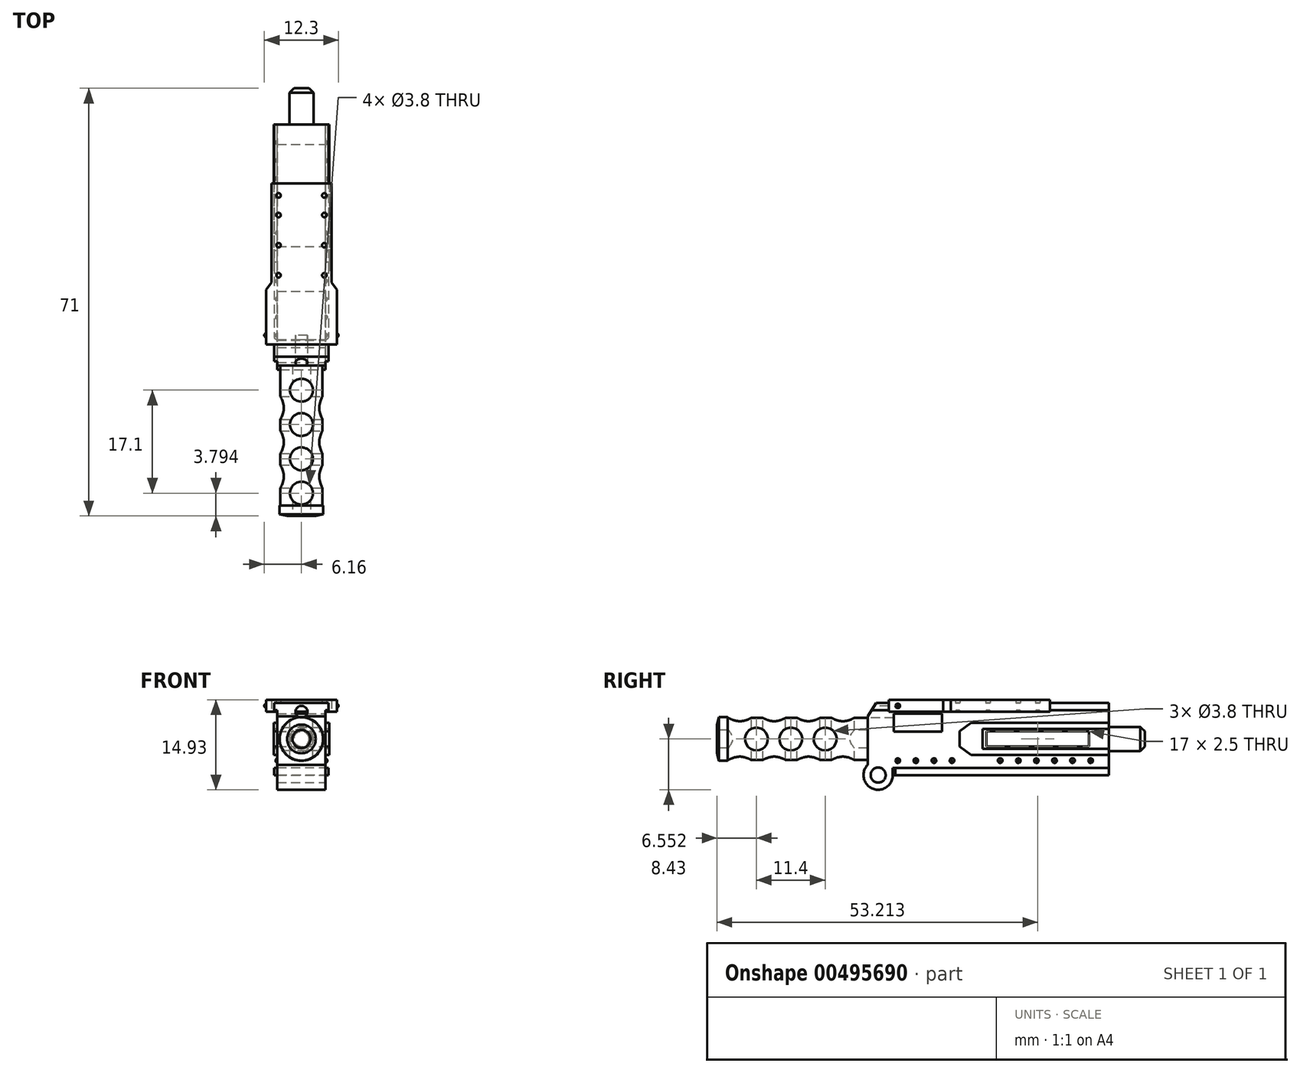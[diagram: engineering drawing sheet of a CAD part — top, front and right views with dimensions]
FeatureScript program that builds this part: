
annotation { "Feature Type Name" : "Feature", "Feature Type Description" : "" }
export const myFeature = defineFeature(function(context is Context, id is Id, definition is map)
    precondition{}
    {
        {
            var Q0;
            Q0=qCreatedBy(makeId("Front.planeOp"),FACE);
            var sketch = newSketch(context, id + "F0", { "sketchPlane" : qUnion([Q0])});
            skLineSegment(sketch, "E0.bottom", {"start": v(4, 6) * mm, "end": v(-4, 6) * mm});
            skLineSegment(sketch, "E0.top", {"start": v(4, -6) * mm, "end": v(-4, -6) * mm});
            skLineSegment(sketch, "E0.left", {"start": v(4, 6) * mm, "end": v(4, -6) * mm});
            skLineSegment(sketch, "E0.right", {"start": v(-4, 6) * mm, "end": v(-4, -6) * mm});
            skPoint(sketch, "E0.middle", {"position": v(0, 0) * mm});
            skSolve(sketch);
        }
        {
            var Q0;
            Q0=makeQuery(id+"F0.imprint","IMPRINT",FACE,{"disambiguationData":[TD([[makeQuery(id+"F0.imprint","IMPRINT",EDGE,{"derivedFrom":sQuery(id+"F0.wireOp",EDGE,"E0.bottom")}),1.0]])]});
            extrude(context, id + "F1", {"entities" : qUnion([Q0]), "depth" : 40 * mm});
        }
        {
            var Q0;
            Q0=makeQuery(id+"F1.opExtrude","CAP_FACE",FACE,{"disambiguationData":[OSD([sQuery(id+"F0.wireOp",EDGE,"E0.bottom"),sQuery(id+"F0.wireOp",EDGE,"E0.top"),sQuery(id+"F0.wireOp",EDGE,"E0.left"),sQuery(id+"F0.wireOp",EDGE,"E0.right")])],"isStart":false});
            var sketch = newSketch(context, id + "F2", { "sketchPlane" : qUnion([Q0])});
            skCircle(sketch, "E1", {"center": v(0, 0) * mm, "radius": 3.5 * mm});
            skSolve(sketch);
        }
        {
            var Q0;
            Q0=qSketchRegion(id+"F2",true);
            extrude(context, id + "F3", {"entities" : qUnion([Q0]), "operationType" : NewBodyOperationType.ADD, "depth" : 25 * mm});
        }
        {
            var Q0;
            Q0=makeQuery(id+"F3.opExtrude","CAP_FACE",FACE,{"disambiguationData":[OSD([sQuery(id+"F2.wireOp",EDGE,"E1")])],"isStart":false});
            var sketch = newSketch(context, id + "F4", { "sketchPlane" : qUnion([Q0])});
            skCircle(sketch, "E2", {"center": v(0, 0) * mm, "radius": 1.5 * mm});
            skSolve(sketch);
        }
        {
            var Q0;
            Q0=makeQuery(id+"F4.imprint","IMPRINT",FACE,{"disambiguationData":[TD([[makeQuery(id+"F4.imprint","IMPRINT",EDGE,{"derivedFrom":sQuery(id+"F4.wireOp",EDGE,"E2")}),-1.0]])]});
            var sketch = newSketch(context, id + "F5", { "sketchPlane" : qUnion([Q0])});
            skCircle(sketch, "E3", {"center": v(0, 0) * mm, "radius": 3.62 * mm});
            skSolve(sketch);
        }
        {
            var Q0;
            Q0=qSketchRegion(id+"F5",true);
            extrude(context, id + "F6", {"entities" : qUnion([Q0]), "operationType" : NewBodyOperationType.ADD, "oppositeDirection" : true, "depth" : 1.75 * mm, "offsetDistance" : 25 * mm});
        }
        {
            var Q0;
            Q0=qSketchRegion(id+"F4",true);
            var Q1;
            Q1=makeQuery(id+"F1.opExtrude","CAP_FACE",FACE,{"disambiguationData":[OSD([sQuery(id+"F0.wireOp",EDGE,"E0.bottom"),sQuery(id+"F0.wireOp",EDGE,"E0.top"),sQuery(id+"F0.wireOp",EDGE,"E0.left"),sQuery(id+"F0.wireOp",EDGE,"E0.right")])],"isStart":false});
            extrude(context, id + "F7", {"entities" : qUnion([Q0]), "operationType" : NewBodyOperationType.REMOVE, "endBound" : BoundingType.UP_TO_SURFACE, "oppositeDirection" : true, "endBoundEntityFace" : qUnion([Q1]), "offsetDistance" : 25 * mm, "depth" : 35 * mm, "hasSecondDirection" : true, "secondDirectionOppositeDirection" : false, "secondDirectionDepth" : .5 * mm});
        }
        {
            var Q0;
            Q0=makeQuery(id+"F1.opExtrude","SWEPT_FACE",FACE,{"disambiguationData":[OSD([sQuery(id+"F0.wireOp",EDGE,"E0.left")])]});
            var sketch = newSketch(context, id + "F8", { "sketchPlane" : qUnion([Q0])});
            skCircle(sketch, "E4", {"center": v(-38.25, -6) * mm, "radius": 2.43 * mm});
            skSolve(sketch);
        }
        {
            var Q0;
            {var subQ0=sQuery(id+"F0.wireOp",EDGE,"E0.left");var subQ1=makeQuery(id+"F1.opExtrude","CAP_EDGE",EDGE,{"disambiguationData":[OSD([subQ0])],"isStart":false});var subQ4=sQuery(id+"F8.wireOp",EDGE,"E4");var subQ5=makeQuery(id+"F8.imprint","INTERSECT",VERTEX,{"derivedFrom":[subQ1,subQ4]});Q0=makeQuery(id+"F8.imprint","IMPRINT",FACE,{"disambiguationData":[TD([[makeQuery(id+"F8.imprint","IMPRINT",EDGE,{"disambiguationData":[TD([[subQ5,-1.0]])],"derivedFrom":subQ4}),1.0]])]});}
            extrude(context, id + "F9", {"entities" : qUnion([Q0]), "operationType" : NewBodyOperationType.ADD, "oppositeDirection" : true, "depth" : 8 * mm});
        }
        {
            var Q0;
            {var subQ0=sQuery(id+"F0.wireOp",EDGE,"E0.left");Q0=makeQuery(id+"F9.boolean.opBoolean","MERGE",FACE,{"derivedFrom":[makeQuery(id+"F1.opExtrude","SWEPT_FACE",FACE,{"disambiguationData":[OSD([subQ0])]}),makeQuery(id+"F9.opExtrude","CAP_FACE",FACE,{"disambiguationData":[OSD([sQuery(id+"F0.wireOp",EDGE,"E0.top"),subQ0,sQuery(id+"F8.wireOp",EDGE,"E4")])],"isStart":true})]});}
            var sketch = newSketch(context, id + "F10", { "sketchPlane" : qUnion([Q0])});
            skCircle(sketch, "E5", {"center": v(-38.25, -6) * mm, "radius": 1.25 * mm});
            skSolve(sketch);
        }
        {
            var Q0;
            Q0=qSketchRegion(id+"F10",true);
            extrude(context, id + "F11", {"entities" : qUnion([Q0]), "operationType" : NewBodyOperationType.REMOVE, "endBound" : BoundingType.THROUGH_ALL, "oppositeDirection" : true, "depth" : 25 * mm});
        }
        {
            var Q0;
            {var subQ0=sQuery(id+"F0.wireOp",EDGE,"E0.left");Q0=makeQuery(id+"F9.boolean.opBoolean","MERGE",FACE,{"derivedFrom":[makeQuery(id+"F1.opExtrude","SWEPT_FACE",FACE,{"disambiguationData":[OSD([subQ0])]}),makeQuery(id+"F9.opExtrude","CAP_FACE",FACE,{"disambiguationData":[OSD([sQuery(id+"F0.wireOp",EDGE,"E0.top"),subQ0,sQuery(id+"F8.wireOp",EDGE,"E4")])],"isStart":true})]});}
            var sketch = newSketch(context, id + "F12", { "sketchPlane" : qUnion([Q0])});
            skLineSegment(sketch, "E6", {"start": v(-40, 6) * mm, "end": v(-35.67, 6) * mm});
            skLineSegment(sketch, "E7", {"start": v(-35.67, 6) * mm, "end": v(-35.67, 4.2) * mm});
            skLineSegment(sketch, "E8.bottom", {"start": v(-35.67, 4.2) * mm, "end": v(-27.67, 4.2) * mm});
            skLineSegment(sketch, "E8.top", {"start": v(-35.67, 1.2) * mm, "end": v(-27.67, 1.2) * mm});
            skLineSegment(sketch, "E8.left", {"start": v(-35.67, 4.2) * mm, "end": v(-35.67, 1.2) * mm});
            skLineSegment(sketch, "E8.right", {"start": v(-27.67, 4.2) * mm, "end": v(-27.67, 1.2) * mm});
            skLineSegment(sketch, "E9.bottom", {"start": v(-20.29, -1.25) * mm, "end": v(-3.29, -1.25) * mm});
            skLineSegment(sketch, "E9.top", {"start": v(-20.29, 1.25) * mm, "end": v(-3.29, 1.25) * mm});
            skLineSegment(sketch, "E9.left", {"start": v(-20.29, -1.25) * mm, "end": v(-20.29, 1.25) * mm});
            skLineSegment(sketch, "E9.right", {"start": v(-3.29, -1.25) * mm, "end": v(-3.29, 1.25) * mm});
            skPoint(sketch, "E9.middle", {"position": v(-11.79, 0) * mm});
            skSolve(sketch);
        }
        {
            var Q0;
            Q0=makeQuery(id+"F12.imprint","IMPRINT",FACE,{"disambiguationData":[TD([[makeQuery(id+"F12.imprint","IMPRINT",EDGE,{"derivedFrom":sQuery(id+"F12.wireOp",EDGE,"E9.bottom")}),1.0]])]});
            var Q1;
            Q1=makeQuery(id+"F12.imprint","IMPRINT",FACE,{"disambiguationData":[TD([[makeQuery(id+"F12.imprint","IMPRINT",EDGE,{"derivedFrom":sQuery(id+"F12.wireOp",EDGE,"E8.bottom")}),-1.0]])]});
            extrude(context, id + "F13", {"entities" : qUnion([Q0, Q1]), "operationType" : NewBodyOperationType.REMOVE, "endBound" : BoundingType.THROUGH_ALL, "oppositeDirection" : true, "depth" : 25 * mm});
        }
        {
            var Q0;
            Q0=makeQuery(id+"F1.opExtrude","SWEPT_FACE",FACE,{"disambiguationData":[OSD([sQuery(id+"F0.wireOp",EDGE,"E0.bottom")])]});
            var sketch = newSketch(context, id + "F14", { "sketchPlane" : qUnion([Q0])});
            skLineSegment(sketch, "E10", {"start": v(4, -29.35) * mm, "end": v(-4, -29.35) * mm, "construction": true});
            skLineSegment(sketch, "E11", {"start": v(4, -29.35) * mm, "end": v(4.5, -29.35) * mm});
            skLineSegment(sketch, "E12", {"start": v(-4, -29.35) * mm, "end": v(-4.5, -29.35) * mm});
            skLineSegment(sketch, "E13.bottom", {"start": v(4.5, -40) * mm, "end": v(-4.5, -40) * mm});
            skLineSegment(sketch, "E13.top", {"start": v(4.5, 0) * mm, "end": v(-4.5, 0) * mm});
            skLineSegment(sketch, "E13.left", {"start": v(4.5, -40) * mm, "end": v(4.5, 0) * mm});
            skLineSegment(sketch, "E13.right", {"start": v(-4.5, -40) * mm, "end": v(-4.5, 0) * mm});
            skSolve(sketch);
        }
        {
            var Q0;
            Q0=qSketchRegion(id+"F14",true);
            extrude(context, id + "F15", {"entities" : qUnion([Q0]), "operationType" : NewBodyOperationType.ADD, "oppositeDirection" : true, "depth" : 1.2 * mm});
        }
        {
            var Q0;
            Q0=makeQuery(id+"F1.opExtrude","SWEPT_FACE",FACE,{"disambiguationData":[OSD([sQuery(id+"F0.wireOp",EDGE,"E0.top")])]});
            var sketch = newSketch(context, id + "F16", { "sketchPlane" : qUnion([Q0])});
            skLineSegment(sketch, "E14", {"start": v(4, 0) * mm, "end": v(4.5, 0) * mm});
            skLineSegment(sketch, "E15", {"start": v(-4, 35.82) * mm, "end": v(-4.5, 35.82) * mm});
            skLineSegment(sketch, "E16.bottom", {"start": v(4.5, 0) * mm, "end": v(-4.5, 0) * mm});
            skLineSegment(sketch, "E16.top", {"start": v(4.5, 35.82) * mm, "end": v(-4.5, 35.82) * mm});
            skLineSegment(sketch, "E16.left", {"start": v(4.5, 0) * mm, "end": v(4.5, 35.82) * mm});
            skLineSegment(sketch, "E16.right", {"start": v(-4.5, 0) * mm, "end": v(-4.5, 35.82) * mm});
            skLineSegment(sketch, "E17", {"start": v(4, 35.82) * mm, "end": v(4.5, 35.38) * mm});
            skLineSegment(sketch, "E18", {"start": v(-4.5, 35.38) * mm, "end": v(-4, 35.82) * mm});
            skSolve(sketch);
        }
        {
            var Q0;
            {var subQ4=sQuery(id+"F16.wireOp",EDGE,"E17");Q0=makeQuery(id+"F16.imprint","IMPRINT",FACE,{"disambiguationData":[TD([[makeQuery(id+"F16.imprint","IMPRINT",EDGE,{"derivedFrom":subQ4}),-1.0]])]});}
            var Q1;
            {var subQ1=sQuery(id+"F0.wireOp",EDGE,"E0.top");var subQ2=makeQuery(id+"F1.opExtrude","SWEPT_EDGE",EDGE,{"disambiguationData":[OSD([subQ1,sQuery(id+"F0.wireOp",EDGE,"E0.left")])]});Q1=makeQuery(id+"F16.imprint","IMPRINT",FACE,{"disambiguationData":[TD([[makeQuery(id+"F16.imprint","IMPRINT",EDGE,{"derivedFrom":subQ2}),-1.0]])]});}
            var Q2;
            {var subQ4=sQuery(id+"F16.wireOp",EDGE,"E18");Q2=makeQuery(id+"F16.imprint","IMPRINT",FACE,{"disambiguationData":[TD([[makeQuery(id+"F16.imprint","IMPRINT",EDGE,{"derivedFrom":subQ4}),-1.0]])]});}
            extrude(context, id + "F17", {"entities" : qUnion([Q0, Q1, Q2]), "operationType" : NewBodyOperationType.ADD, "oppositeDirection" : true, "depth" : 1.2 * mm});
        }
        {
            var Q0;
            Q0=makeQuery(id+"F15.boolean.opBoolean","MERGE",FACE,{"derivedFrom":[makeQuery(id+"F1.opExtrude","CAP_FACE",FACE,{"disambiguationData":[OSD([sQuery(id+"F0.wireOp",EDGE,"E0.bottom"),sQuery(id+"F0.wireOp",EDGE,"E0.top"),sQuery(id+"F0.wireOp",EDGE,"E0.left"),sQuery(id+"F0.wireOp",EDGE,"E0.right")])],"isStart":false}),makeQuery(id+"F15.opExtrude","SWEPT_FACE",FACE,{"disambiguationData":[OSD([sQuery(id+"F14.wireOp",EDGE,"E13.bottom")])]})]});
            var sketch = newSketch(context, id + "F18", { "sketchPlane" : qUnion([Q0])});
            skPoint(sketch, "E19.endSnap0", {"position": v(0, 6) * mm});
            skCircle(sketch, "E20", {"center": v(0, 4.5) * mm, "radius": 1 * mm});
            skSolve(sketch);
        }
        {
            var Q0;
            Q0=makeQuery(id+"F18.imprint","IMPRINT",FACE,{"disambiguationData":[TD([[makeQuery(id+"F18.imprint","IMPRINT",EDGE,{"derivedFrom":sQuery(id+"F18.wireOp",EDGE,"E20")}),1.0]])]});
            var Q1;
            Q1=sQuery(id+"F18.wireOp",EDGE,"E20");
            extrude(context, id + "F19", {"entities" : qUnion([Q0]), "operationType" : NewBodyOperationType.REMOVE, "surfaceEntities" : qUnion([Q1]), "oppositeDirection" : true, "offsetDistance" : 25 * mm, "depth" : 5 * mm});
        }
        {
            var Q0;
            Q0=makeQuery(id+"F10.imprint","IMPRINT",FACE,{"disambiguationData":[TD([[makeQuery(id+"F10.imprint","IMPRINT",EDGE,{"derivedFrom":sQuery(id+"F10.wireOp",EDGE,"E5")}),-1.0]])]});
            var sketch = newSketch(context, id + "F20", { "sketchPlane" : qUnion([Q0])});
            skLineSegment(sketch, "E21", {"start": v(0, 1.65) * mm, "end": v(-20.95, 1.65) * mm});
            skLineSegment(sketch, "E22", {"start": v(-20.95, 1.65) * mm, "end": v(-20.95, 0) * mm});
            skLineSegment(sketch, "E23.MirrorCS", {"start": v(0, -1.65) * mm, "end": v(-20.95, -1.65) * mm});
            skLineSegment(sketch, "E24.MirrorCS", {"start": v(-20.95, -1.65) * mm, "end": v(-20.95, 0) * mm});
            skLineSegment(sketch, "E25", {"start": v(0, 1.65) * mm, "end": v(0, 2.68) * mm});
            skLineSegment(sketch, "E26", {"start": v(0, 2.68) * mm, "end": v(-22.85, 2.68) * mm});
            skLineSegment(sketch, "E27", {"start": v(-22.85, 2.68) * mm, "end": v(-24.71, 1.26) * mm});
            skLineSegment(sketch, "E28", {"start": v(-24.71, 1.26) * mm, "end": v(-24.71, 0) * mm});
            skLineSegment(sketch, "E29.MirrorCS", {"start": v(0, -2.68) * mm, "end": v(-22.85, -2.68) * mm});
            skLineSegment(sketch, "E30.MirrorCS", {"start": v(-22.85, -2.68) * mm, "end": v(-24.71, -1.26) * mm});
            skLineSegment(sketch, "E31.MirrorCS", {"start": v(-24.71, -1.26) * mm, "end": v(-24.71, 0) * mm});
            skLineSegment(sketch, "E32", {"start": v(0, -2.68) * mm, "end": v(0, -1.65) * mm});
            skSolve(sketch);
        }
        {
            var Q0;
            Q0=qSketchRegion(id+"F20",true);
            extrude(context, id + "F21", {"entities" : qUnion([Q0]), "operationType" : NewBodyOperationType.ADD, "depth" : .6 * mm, "hasSecondDirection" : true, "secondDirectionOppositeDirection" : true, "secondDirectionDepth" : 8.6 * mm});
        }
        {
            var Q0;
            Q0=makeQuery(id+"F21.boolean.opBoolean","MERGE",FACE,{"derivedFrom":[makeQuery(id+"F17.boolean.opBoolean","MERGE",FACE,{"derivedFrom":[makeQuery(id+"F15.boolean.opBoolean","MERGE",FACE,{"derivedFrom":[makeQuery(id+"F1.opExtrude","CAP_FACE",FACE,{"disambiguationData":[OSD([sQuery(id+"F0.wireOp",EDGE,"E0.bottom"),sQuery(id+"F0.wireOp",EDGE,"E0.top"),sQuery(id+"F0.wireOp",EDGE,"E0.left"),sQuery(id+"F0.wireOp",EDGE,"E0.right")])],"isStart":true}),makeQuery(id+"F15.opExtrude","SWEPT_FACE",FACE,{"disambiguationData":[OSD([sQuery(id+"F14.wireOp",EDGE,"E13.top")])]})]}),makeQuery(id+"F17.opExtrude","SWEPT_FACE",FACE,{"disambiguationData":[OSD([sQuery(id+"F16.wireOp",EDGE,"E16.bottom")])]})]}),makeQuery(id+"F21.opExtrude","SWEPT_FACE",FACE,{"disambiguationData":[OSD([sQuery(id+"F20.wireOp",EDGE,"E25")])]}),makeQuery(id+"F21.opExtrude","SWEPT_FACE",FACE,{"disambiguationData":[OSD([sQuery(id+"F20.wireOp",EDGE,"E32")])]})]});
            var sketch = newSketch(context, id + "F22", { "sketchPlane" : qUnion([Q0])});
            skCircle(sketch, "E33", {"center": v(0, 0) * mm, "radius": 2 * mm});
            skSolve(sketch);
        }
        {
            var Q0;
            Q0=qCreatedBy(makeId("Top.planeOp"),FACE);
            var sketch = newSketch(context, id + "F23", { "sketchPlane" : qUnion([Q0])});
            skLineSegment(sketch, "E34", {"start": v(0, -65) * mm, "end": v(0, -63.1) * mm});
            skLineSegment(sketch, "E35", {"start": v(0, -63.1) * mm, "end": v(0, -61.2) * mm});
            skLineSegment(sketch, "E36", {"start": v(0, -61.2) * mm, "end": v(0, -59.3) * mm});
            skLineSegment(sketch, "E37", {"start": v(0, -59.3) * mm, "end": v(0, -57.4) * mm});
            skLineSegment(sketch, "E38", {"start": v(0, -57.4) * mm, "end": v(0, -55.5) * mm});
            skLineSegment(sketch, "E39", {"start": v(0, -55.5) * mm, "end": v(0, -53.6) * mm});
            skLineSegment(sketch, "E40", {"start": v(0, -53.6) * mm, "end": v(0, -51.7) * mm});
            skLineSegment(sketch, "E41", {"start": v(0, -51.7) * mm, "end": v(0, -49.8) * mm});
            skLineSegment(sketch, "E42", {"start": v(0, -49.8) * mm, "end": v(0, -47.9) * mm});
            skLineSegment(sketch, "E43", {"start": v(0, -47.9) * mm, "end": v(0, -46) * mm});
            skLineSegment(sketch, "E44", {"start": v(0, -46) * mm, "end": v(0, -44.1) * mm});
            skLineSegment(sketch, "E45", {"start": v(0, -44.1) * mm, "end": v(0, -42.2) * mm});
            skCircle(sketch, "E46", {"center": v(0, -61.2) * mm, "radius": 1.9 * mm});
            skCircle(sketch, "E47", {"center": v(0, -55.5) * mm, "radius": 1.9 * mm});
            skCircle(sketch, "E48", {"center": v(0, -49.8) * mm, "radius": 1.9 * mm});
            skCircle(sketch, "E49", {"center": v(0, -44.1) * mm, "radius": 1.9 * mm});
            skSolve(sketch);
        }
        {
            var Q0;
            Q0=qSketchRegion(id+"F23",true);
            extrude(context, id + "F24", {"entities" : qUnion([Q0]), "operationType" : NewBodyOperationType.REMOVE, "oppositeDirection" : true, "depth" : 6 * mm, "hasSecondDirection" : true, "secondDirectionOppositeDirection" : false, "secondDirectionDepth" : 6 * mm});
        }
        {
            var Q0;
            Q0=qCreatedBy(makeId("Right.planeOp"),FACE);
            var sketch = newSketch(context, id + "F25", { "sketchPlane" : qUnion([Q0])});
            skLineSegment(sketch, "E50", {"start": v(-81.72, 0) * mm, "end": v(-78.97, 0) * mm});
            skLineSegment(sketch, "E51", {"start": v(-65, 0) * mm, "end": v(-62.25, 0) * mm});
            skLineSegment(sketch, "E52", {"start": v(-62.25, 0) * mm, "end": v(-60.35, 0) * mm});
            skLineSegment(sketch, "E53", {"start": v(-60.35, 0) * mm, "end": v(-58.45, 0) * mm});
            skLineSegment(sketch, "E54", {"start": v(-58.45, 0) * mm, "end": v(-56.55, 0) * mm});
            skLineSegment(sketch, "E55", {"start": v(-56.55, 0) * mm, "end": v(-54.65, 0) * mm});
            skLineSegment(sketch, "E56", {"start": v(-54.65, 0) * mm, "end": v(-52.75, 0) * mm});
            skLineSegment(sketch, "E57", {"start": v(-52.75, 0) * mm, "end": v(-50.85, 0) * mm});
            skLineSegment(sketch, "E58", {"start": v(-50.85, 0) * mm, "end": v(-48.95, 0) * mm});
            skLineSegment(sketch, "E59", {"start": v(-48.95, 0) * mm, "end": v(-47.05, 0) * mm});
            skLineSegment(sketch, "E60", {"start": v(-47.05, 0) * mm, "end": v(-45.15, 0) * mm});
            skCircle(sketch, "E61", {"center": v(-58.45, 0) * mm, "radius": 1.9 * mm});
            skCircle(sketch, "E62", {"center": v(-52.75, 0) * mm, "radius": 1.9 * mm});
            skCircle(sketch, "E63", {"center": v(-47.05, 0) * mm, "radius": 1.9 * mm});
            skLineSegment(sketch, "E64", {"start": v(-47.05, 0) * mm, "end": v(-47.05, 4.24) * mm});
            skSolve(sketch);
        }
        {
            var Q0;
            Q0=qSketchRegion(id+"F25",true);
            extrude(context, id + "F26", {"entities" : qUnion([Q0]), "operationType" : NewBodyOperationType.REMOVE, "endBound" : BoundingType.THROUGH_ALL, "oppositeDirection" : true, "depth" : 25 * mm, "hasSecondDirection" : true, "secondDirectionOppositeDirection" : false, "secondDirectionDepth" : 25 * mm});
        }
        {
            var Q0;
            Q0=qSketchRegion(id+"F22",true);
            extrude(context, id + "F27", {"entities" : qUnion([Q0]), "operationType" : NewBodyOperationType.ADD, "offsetDistance" : 25 * mm, "depth" : 6 * mm});
        }
        {
            var Q0;
            Q0=makeQuery(id+"F10.imprint","IMPRINT",FACE,{"disambiguationData":[TD([[makeQuery(id+"F10.imprint","IMPRINT",EDGE,{"derivedFrom":sQuery(id+"F10.wireOp",EDGE,"E5")}),-1.0]])]});
            var sketch = newSketch(context, id + "F28", { "sketchPlane" : qUnion([Q0])});
            skLineSegment(sketch, "E65", {"start": v(-40.01, 3.72) * mm, "end": v(-38.55, 6.02) * mm});
            skLineSegment(sketch, "E66", {"start": v(-38.55, 6.02) * mm, "end": v(-40.05, 6.02) * mm});
            skLineSegment(sketch, "E67", {"start": v(-40.05, 6.02) * mm, "end": v(-40.01, 3.72) * mm});
            skSolve(sketch);
        }
        {
            var Q0;
            Q0=qSketchRegion(id+"F28",true);
            extrude(context, id + "F29", {"entities" : qUnion([Q0]), "operationType" : NewBodyOperationType.REMOVE, "endBound" : BoundingType.THROUGH_ALL, "oppositeDirection" : true, "depth" : 25 * mm, "hasSecondDirection" : true, "secondDirectionBound" : SecondDirectionBoundingType.THROUGH_ALL, "secondDirectionOppositeDirection" : false, "secondDirectionDepth" : 25 * mm});
        }
        {
            var Q0;
            {var subQ1=sQuery(id+"F0.wireOp",EDGE,"E0.bottom");var subQ2=makeQuery(id+"F1.opExtrude","SWEPT_EDGE",EDGE,{"disambiguationData":[OSD([subQ1,sQuery(id+"F0.wireOp",EDGE,"E0.left")])]});var subQ7=sQuery(id+"F14.wireOp",EDGE,"E13.bottom");var subQ8=makeQuery(id+"F14.imprint","INTERSECT",VERTEX,{"derivedFrom":[subQ2,subQ7]});Q0=makeQuery(id+"F14.imprint","IMPRINT",FACE,{"disambiguationData":[TD([[makeQuery(id+"F14.imprint","IMPRINT",EDGE,{"disambiguationData":[TD([[subQ8,-1.0]])],"derivedFrom":subQ7}),-1.0]])]});}
            var sketch = newSketch(context, id + "F30", { "sketchPlane" : qUnion([Q0])});
            skLineSegment(sketch, "E68", {"start": v(0, -9.78) * mm, "end": v(-5, -9.78) * mm});
            skLineSegment(sketch, "E69", {"start": v(-5, -9.78) * mm, "end": v(-5, -26.2) * mm});
            skLineSegment(sketch, "E70", {"start": v(-5, -26.2) * mm, "end": v(-5.86, -27.45) * mm});
            skLineSegment(sketch, "E71", {"start": v(-5.86, -27.45) * mm, "end": v(-5.86, -36.5) * mm});
            skLineSegment(sketch, "E72", {"start": v(-5.86, -36.5) * mm, "end": v(0, -36.5) * mm});
            skLineSegment(sketch, "E73", {"start": v(0, 0) * mm, "end": v(0, -16.84) * mm, "construction": true});
            skLineSegment(sketch, "E74.MirrorCS", {"start": v(0, -9.78) * mm, "end": v(5, -9.78) * mm});
            skLineSegment(sketch, "E75.MirrorCS", {"start": v(5, -9.78) * mm, "end": v(5, -26.2) * mm});
            skLineSegment(sketch, "E76.MirrorCS", {"start": v(5.86, -36.5) * mm, "end": v(0, -36.5) * mm});
            skLineSegment(sketch, "E77.MirrorCS", {"start": v(5.86, -27.45) * mm, "end": v(5.86, -36.5) * mm});
            skLineSegment(sketch, "E78.MirrorCS", {"start": v(5, -26.2) * mm, "end": v(5.86, -27.45) * mm});
            skLineSegment(sketch, "E79", {"start": v(0, -9.78) * mm, "end": v(5, -9.78) * mm, "construction": true});
            skLineSegment(sketch, "E80", {"start": v(0, -9.78) * mm, "end": v(0, -11.78) * mm, "construction": true});
            skLineSegment(sketch, "E81", {"start": v(0, -11.78) * mm, "end": v(3.8, -11.78) * mm, "construction": true});
            skLineSegment(sketch, "E82", {"start": v(3.8, -11.78) * mm, "end": v(3.8, -15.04) * mm, "construction": true});
            skLineSegment(sketch, "E83", {"start": v(3.8, -15.04) * mm, "end": v(3.8, -17.54) * mm, "construction": true});
            skLineSegment(sketch, "E84", {"start": v(3.8, -17.54) * mm, "end": v(3.8, -20.04) * mm, "construction": true});
            skLineSegment(sketch, "E85", {"start": v(3.8, -20.04) * mm, "end": v(3.8, -22.54) * mm, "construction": true});
            skLineSegment(sketch, "E86", {"start": v(3.8, -22.54) * mm, "end": v(3.8, -25.04) * mm, "construction": true});
            skCircle(sketch, "E87", {"center": v(3.8, -11.78) * mm, "radius": 0.38 * mm});
            skCircle(sketch, "E88", {"center": v(3.8, -15.04) * mm, "radius": 0.38 * mm});
            skCircle(sketch, "E89", {"center": v(3.8, -20.04) * mm, "radius": 0.38 * mm});
            skCircle(sketch, "E90", {"center": v(3.8, -25.04) * mm, "radius": 0.38 * mm});
            skCircle(sketch, "E91.MirrorC", {"center": v(-3.8, -11.78) * mm, "radius": 0.38 * mm});
            skCircle(sketch, "E92.MirrorC", {"center": v(-3.8, -15.04) * mm, "radius": 0.38 * mm});
            skCircle(sketch, "E93.MirrorC", {"center": v(-3.8, -20.04) * mm, "radius": 0.38 * mm});
            skCircle(sketch, "E94.MirrorC", {"center": v(-3.8, -25.04) * mm, "radius": 0.38 * mm});
            skSolve(sketch);
        }
        {
            var Q0;
            Q0=qSketchRegion(id+"F30",true);
            extrude(context, id + "F31", {"entities" : qUnion([Q0]), "operationType" : NewBodyOperationType.ADD, "depth" : 0.5 * mm, "offsetDistance" : 25 * mm, "hasSecondDirection" : true, "secondDirectionOppositeDirection" : true, "secondDirectionDepth" : 1.5 * mm});
        }
        {
            var Q0;
            Q0=makeQuery(id+"F31.opExtrude","SWEPT_FACE",FACE,{"disambiguationData":[OSD([sQuery(id+"F30.wireOp",EDGE,"E71")])]});
            var sketch = newSketch(context, id + "F32", { "sketchPlane" : qUnion([Q0])});
            skLineSegment(sketch, "E95", {"start": v(36.5, 4.5) * mm, "end": v(36.5, 5.5) * mm, "construction": true});
            skLineSegment(sketch, "E96", {"start": v(36.5, 5.5) * mm, "end": v(35, 5.5) * mm, "construction": true});
            skCircle(sketch, "E97", {"center": v(35, 5.5) * mm, "radius": 0.38 * mm});
            skSolve(sketch);
        }
        {
            var Q0;
            Q0=makeQuery(id+"F32.imprint","IMPRINT",FACE,{"disambiguationData":[TD([[makeQuery(id+"F32.imprint","IMPRINT",EDGE,{"derivedFrom":sQuery(id+"F32.wireOp",EDGE,"E97")}),1.0]])]});
            extrude(context, id + "F33", {"entities" : qUnion([Q0]), "operationType" : NewBodyOperationType.ADD, "depth" : 0.3 * mm, "offsetDistance" : 25 * mm, "hasSecondDirection" : true, "secondDirectionOppositeDirection" : true, "secondDirectionDepth" : 12 * mm});
        }
        {
            var Q0;
            Q0=makeQuery(id+"F33.opExtrude","CAP_EDGE",EDGE,{"disambiguationData":[OSD([sQuery(id+"F32.wireOp",EDGE,"E97")])],"isStart":false});
            var Q1;
            Q1=makeQuery(id+"F33.opExtrude","CAP_EDGE",EDGE,{"disambiguationData":[OSD([sQuery(id+"F32.wireOp",EDGE,"E97")])],"isStart":true});
            fillet(context, id + "F34", {"entities" : qUnion([Q0, Q1]), "tangentPropagation" : true, "crossSection" : FilletCrossSection.CONIC, "radius" : 0.3 * mm, "rho" : 0.25, "defaultsChanged" : false, "vertexSettings" : [], "allowEdgeOverflow" : false});
        }
        {
            var Q0;
            Q0=makeQuery(id+"F27.opExtrude","CAP_EDGE",EDGE,{"disambiguationData":[OSD([sQuery(id+"F22.wireOp",EDGE,"E33")])],"isStart":false});
            chamfer(context, id + "F35", {"entities" : qUnion([Q0]), "width" : 0.75 * mm, "tangentPropagation" : true});
        }
        {
            var Q0;
            Q0=makeQuery(id+"F10.imprint","IMPRINT",FACE,{"disambiguationData":[TD([[makeQuery(id+"F10.imprint","IMPRINT",EDGE,{"derivedFrom":sQuery(id+"F10.wireOp",EDGE,"E5")}),-1.0]])]});
            var sketch = newSketch(context, id + "F36", { "sketchPlane" : qUnion([Q0])});
            skLineSegment(sketch, "E98", {"start": v(0, 0) * mm, "end": v(0, -3.6) * mm, "construction": true});
            skLineSegment(sketch, "E99", {"start": v(0, -3.6) * mm, "end": v(-3, -3.6) * mm, "construction": true});
            skLineSegment(sketch, "E100", {"start": v(-3, -3.6) * mm, "end": v(-6, -3.6) * mm, "construction": true});
            skLineSegment(sketch, "E101", {"start": v(-6, -3.6) * mm, "end": v(-9, -3.6) * mm, "construction": true});
            skLineSegment(sketch, "E102", {"start": v(-9, -3.6) * mm, "end": v(-12, -3.6) * mm, "construction": true});
            skLineSegment(sketch, "E103", {"start": v(-12, -3.6) * mm, "end": v(-15, -3.6) * mm, "construction": true});
            skLineSegment(sketch, "E104", {"start": v(-15, -3.6) * mm, "end": v(-18, -3.6) * mm, "construction": true});
            skLineSegment(sketch, "E105", {"start": v(-18, -3.6) * mm, "end": v(-26, -3.6) * mm, "construction": true});
            skPoint(sketch, "E105.endSnap0", {"position": v(-16.5, -3.6) * mm});
            skLineSegment(sketch, "E106", {"start": v(-26, -3.6) * mm, "end": v(-29, -3.6) * mm, "construction": true});
            skLineSegment(sketch, "E107", {"start": v(-29, -3.6) * mm, "end": v(-32, -3.6) * mm, "construction": true});
            skLineSegment(sketch, "E108", {"start": v(-32, -3.6) * mm, "end": v(-35, -3.6) * mm, "construction": true});
            skCircle(sketch, "E109", {"center": v(-3, -3.6) * mm, "radius": 0.38 * mm});
            skCircle(sketch, "E110", {"center": v(-6, -3.6) * mm, "radius": 0.38 * mm});
            skCircle(sketch, "E111", {"center": v(-9, -3.6) * mm, "radius": 0.38 * mm});
            skCircle(sketch, "E112", {"center": v(-12, -3.6) * mm, "radius": 0.38 * mm});
            skCircle(sketch, "E113", {"center": v(-15, -3.6) * mm, "radius": 0.38 * mm});
            skCircle(sketch, "E114", {"center": v(-18, -3.6) * mm, "radius": 0.38 * mm});
            skCircle(sketch, "E115", {"center": v(-26, -3.6) * mm, "radius": 0.38 * mm});
            skCircle(sketch, "E116", {"center": v(-29, -3.6) * mm, "radius": 0.38 * mm});
            skCircle(sketch, "E117", {"center": v(-32, -3.6) * mm, "radius": 0.37 * mm});
            skCircle(sketch, "E118", {"center": v(-35, -3.6) * mm, "radius": 0.38 * mm});
            skSolve(sketch);
        }
        {
            var Q0;
            Q0=qSketchRegion(id+"F36",true);
            extrude(context, id + "F37", {"entities" : qUnion([Q0]), "operationType" : NewBodyOperationType.ADD, "depth" : 0.3 * mm, "offsetDistance" : 25 * mm, "hasSecondDirection" : true, "secondDirectionOppositeDirection" : true, "secondDirectionDepth" : 8.3 * mm});
        }
        {
            var Q0;
            Q0=makeQuery(id+"F37.opExtrude","CAP_EDGE",EDGE,{"disambiguationData":[OSD([sQuery(id+"F36.wireOp",EDGE,"E118")])],"isStart":false});
            var Q1;
            Q1=makeQuery(id+"F37.opExtrude","CAP_EDGE",EDGE,{"disambiguationData":[OSD([sQuery(id+"F36.wireOp",EDGE,"E117")])],"isStart":false});
            var Q2;
            Q2=makeQuery(id+"F37.opExtrude","CAP_EDGE",EDGE,{"disambiguationData":[OSD([sQuery(id+"F36.wireOp",EDGE,"E116")])],"isStart":false});
            var Q3;
            Q3=makeQuery(id+"F37.opExtrude","CAP_EDGE",EDGE,{"disambiguationData":[OSD([sQuery(id+"F36.wireOp",EDGE,"E115")])],"isStart":false});
            var Q4;
            Q4=makeQuery(id+"F37.opExtrude","CAP_EDGE",EDGE,{"disambiguationData":[OSD([sQuery(id+"F36.wireOp",EDGE,"E114")])],"isStart":false});
            var Q5;
            Q5=makeQuery(id+"F37.opExtrude","CAP_EDGE",EDGE,{"disambiguationData":[OSD([sQuery(id+"F36.wireOp",EDGE,"E113")])],"isStart":false});
            var Q6;
            Q6=makeQuery(id+"F37.opExtrude","CAP_EDGE",EDGE,{"disambiguationData":[OSD([sQuery(id+"F36.wireOp",EDGE,"E112")])],"isStart":false});
            var Q7;
            Q7=makeQuery(id+"F37.opExtrude","CAP_EDGE",EDGE,{"disambiguationData":[OSD([sQuery(id+"F36.wireOp",EDGE,"E111")])],"isStart":false});
            var Q8;
            Q8=makeQuery(id+"F37.opExtrude","CAP_EDGE",EDGE,{"disambiguationData":[OSD([sQuery(id+"F36.wireOp",EDGE,"E110")])],"isStart":false});
            var Q9;
            Q9=makeQuery(id+"F37.opExtrude","CAP_EDGE",EDGE,{"disambiguationData":[OSD([sQuery(id+"F36.wireOp",EDGE,"E109")])],"isStart":false});
            var Q10;
            Q10=makeQuery(id+"F37.opExtrude","CAP_EDGE",EDGE,{"disambiguationData":[OSD([sQuery(id+"F36.wireOp",EDGE,"E109")])],"isStart":true});
            var Q11;
            Q11=makeQuery(id+"F37.opExtrude","CAP_EDGE",EDGE,{"disambiguationData":[OSD([sQuery(id+"F36.wireOp",EDGE,"E110")])],"isStart":true});
            var Q12;
            Q12=makeQuery(id+"F37.opExtrude","CAP_EDGE",EDGE,{"disambiguationData":[OSD([sQuery(id+"F36.wireOp",EDGE,"E111")])],"isStart":true});
            var Q13;
            Q13=makeQuery(id+"F37.opExtrude","CAP_EDGE",EDGE,{"disambiguationData":[OSD([sQuery(id+"F36.wireOp",EDGE,"E112")])],"isStart":true});
            var Q14;
            Q14=makeQuery(id+"F37.opExtrude","CAP_EDGE",EDGE,{"disambiguationData":[OSD([sQuery(id+"F36.wireOp",EDGE,"E113")])],"isStart":true});
            var Q15;
            Q15=makeQuery(id+"F37.opExtrude","CAP_EDGE",EDGE,{"disambiguationData":[OSD([sQuery(id+"F36.wireOp",EDGE,"E114")])],"isStart":true});
            var Q16;
            Q16=makeQuery(id+"F37.opExtrude","CAP_EDGE",EDGE,{"disambiguationData":[OSD([sQuery(id+"F36.wireOp",EDGE,"E115")])],"isStart":true});
            var Q17;
            Q17=makeQuery(id+"F37.opExtrude","CAP_EDGE",EDGE,{"disambiguationData":[OSD([sQuery(id+"F36.wireOp",EDGE,"E116")])],"isStart":true});
            var Q18;
            Q18=makeQuery(id+"F37.opExtrude","CAP_EDGE",EDGE,{"disambiguationData":[OSD([sQuery(id+"F36.wireOp",EDGE,"E117")])],"isStart":true});
            var Q19;
            Q19=makeQuery(id+"F37.opExtrude","CAP_EDGE",EDGE,{"disambiguationData":[OSD([sQuery(id+"F36.wireOp",EDGE,"E118")])],"isStart":true});
            fillet(context, id + "F38", {"entities" : qUnion([Q0, Q1, Q2, Q3, Q4, Q5, Q6, Q7, Q8, Q9, Q10, Q11, Q12, Q13, Q14, Q15, Q16, Q17, Q18, Q19]), "tangentPropagation" : true, "crossSection" : FilletCrossSection.CONIC, "radius" : 0.3 * mm, "rho" : .25, "defaultsChanged" : false, "vertexSettings" : [], "allowEdgeOverflow" : false});
        }
        {
            var Q0;
            Q0=makeQuery(id+"F6.opExtrude","CAP_EDGE",EDGE,{"disambiguationData":[OSD([sQuery(id+"F5.wireOp",EDGE,"E3")])],"isStart":true});
            chamfer(context, id + "F39", {"entities" : qUnion([Q0]), "chamferType" : ChamferType.TWO_OFFSETS, "width1" : 1.25 * mm, "oppositeDirection" : false, "width2" : .3 * mm, "tangentPropagation" : true});
        }
    });
